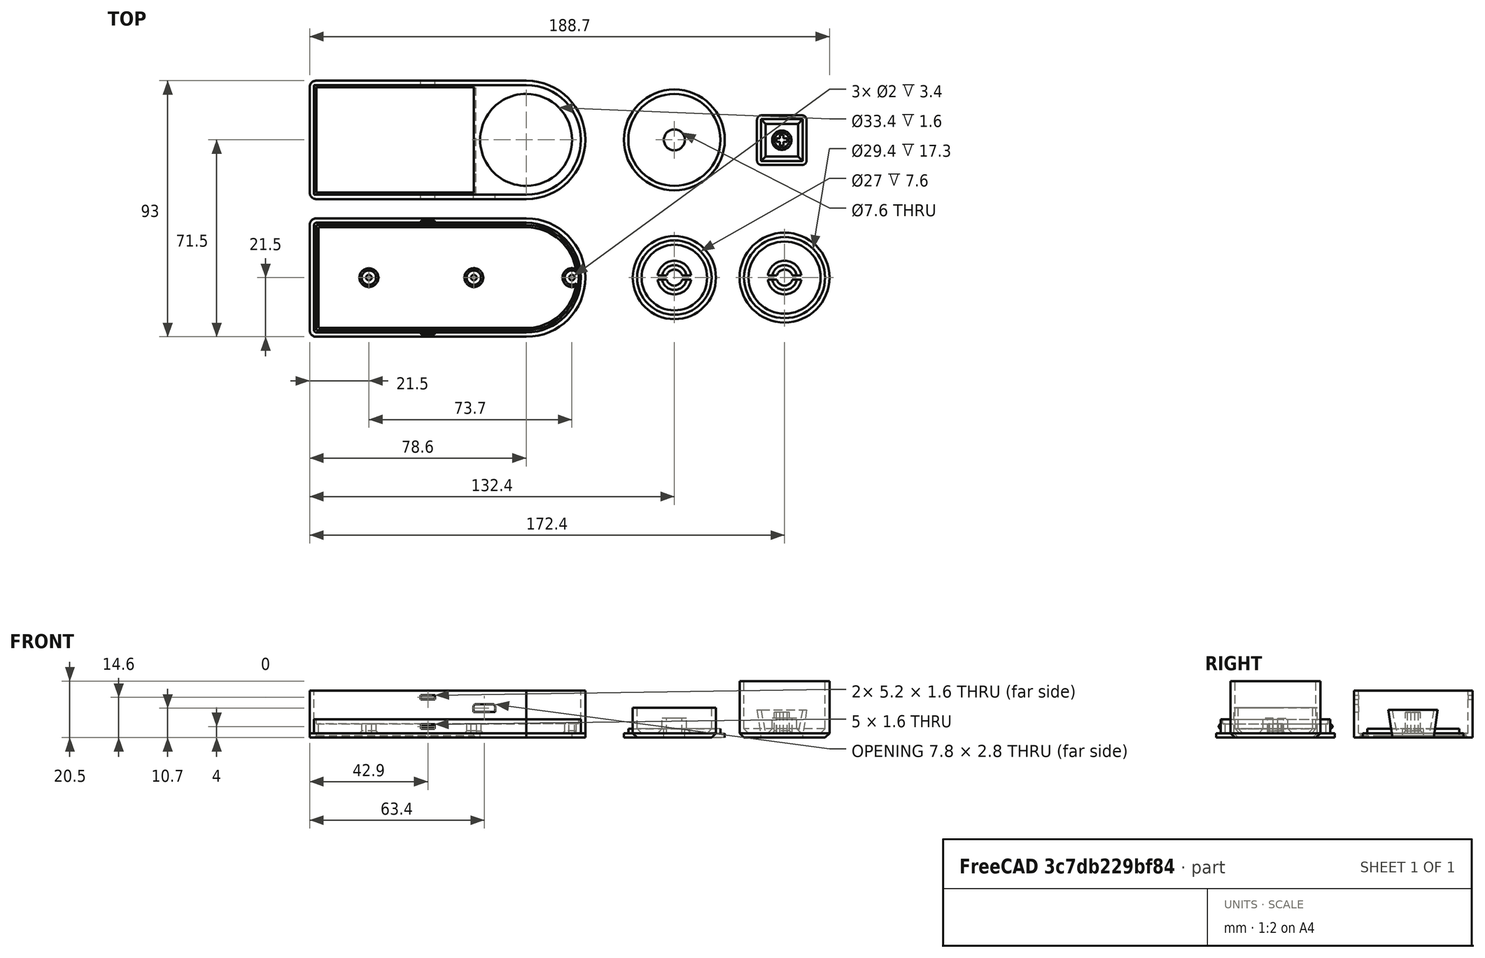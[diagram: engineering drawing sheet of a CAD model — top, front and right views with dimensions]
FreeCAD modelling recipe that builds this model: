
FCSTD DOCUMENT  (FreeCAD 0.16R)
Label: Macropad_plus
License: All rights reserved
LicenseURL: http://en.wikipedia.org/wiki/All_rights_reserved
objects: Part::Cylinder×25, Part::Cut×18, Part::Box×15, Part::MultiFuse×15, Part::Chamfer×13, Part::Fillet×5, Part::Wedge×2
note: 93 computed .brp shape members not serialized (recipe doc carries the construction recipe); baked Part::Feature solids carry a one-line shape summary decoded from their .brp

FEATURE [Part::Box] Box  label="Würfel"
  Height = 1.6
  Length = 78.7
  Placement = pos=(-2.4,-2.4,0) rot=(0,0,1;0rad)
  Width = 43
FEATURE [Part::Box] Box001  label="Würfel001"
  Height = 6.6
  Length = 77.1
  Placement = pos=(-0.8,-0.8,0) rot=(0,0,1;0rad)
  Width = 39.8
FEATURE [Part::Box] Box002  label="Würfel002"
  Height = 1.6
  Length = 76.3
  Placement = pos=(0,0,5) rot=(0,0,1;0rad)
  Width = 38.2
FEATURE [Part::Cylinder] Cylinder  label="Zylinder"
  Angle = 360
  Height = 1.6
  Placement = pos=(76.2,19.1,0) rot=(0,0,1;0rad)
  Radius = 21.5
FEATURE [Part::Cylinder] Cylinder001  label="Zylinder001"
  Angle = 360
  Height = 6.6
  Placement = pos=(76.2,19.1,0) rot=(0,0,1;0rad)
  Radius = 19.9
FEATURE [Part::Cylinder] Cylinder002  label="Zylinder002"
  Angle = 360
  Height = 1.6
  Placement = pos=(76.2,19.1,5) rot=(0,0,1;0rad)
  Radius = 19.1
FEATURE [Part::Box] Box003  label="Würfel003"
  Height = 5
  Length = 75.5
  Placement = pos=(0.8,0.8,1.6) rot=(0,0,1;0rad)
  Width = 36.6
FEATURE [Part::Cylinder] Cylinder003  label="Zylinder003"
  Angle = 360
  Height = 5
  Placement = pos=(76.2,19.1,1.6) rot=(0,0,1;0rad)
  Radius = 18.3
FEATURE [Part::MultiFuse] Fusion
  Shapes = -> [Box,Cylinder]
FEATURE [Part::MultiFuse] Fusion001
  Shapes = -> [Box001,Cylinder001]
FEATURE [Part::MultiFuse] Fusion002
  Shapes = -> [Box002,Cylinder002]
FEATURE [Part::MultiFuse] Fusion003
  Shapes = -> [Box003,Cylinder003]
FEATURE [Part::MultiFuse] Fusion004
  Shapes = -> [Fusion,Fusion001]
FEATURE [Part::MultiFuse] Fusion005
  Shapes = -> [Fusion002,Fusion003]
FEATURE [Part::Cut] Cut
  Base = -> Fusion004
  Tool = -> Fusion005
FEATURE [Part::Fillet] Fillet
  Base = -> Cut
  Edges = 2 edges r=0.8: [Edge30,Edge31]
FEATURE [Part::Fillet] Fillet001
  Base = -> Fillet
  Edges = 2 edges r=2.4: [Edge24,Edge27]
FEATURE [Part::Cylinder] Cylinder004  label="Zylinder004"
  Angle = 360
  Height = 5
  Placement = pos=(19.1,19.1,0) rot=(0,0,1;0rad)
  Radius = 2.6
FEATURE [Part::Cylinder] Cylinder005  label="Zylinder005"
  Angle = 360
  Height = 5
  Placement = pos=(19.1,19.1,1.6) rot=(0,0,1;0rad)
  Radius = 1
FEATURE [Part::Cut] Cut001
  Base = -> Cylinder004
  Tool = -> Cylinder005
FEATURE [Part::Cylinder] Cylinder006  label="Zylinder006"
  Angle = 360
  Height = 5
  Placement = pos=(57.2,19.1,0) rot=(0,0,1;0rad)
  Radius = 2.6
FEATURE [Part::Cylinder] Cylinder007  label="Zylinder007"
  Angle = 360
  Height = 5
  Placement = pos=(57.2,19.1,1.6) rot=(0,0,1;0rad)
  Radius = 1
FEATURE [Part::Cut] Cut002
  Base = -> Cylinder006
  Tool = -> Cylinder007
FEATURE [Part::Cylinder] Cylinder008  label="Zylinder008"
  Angle = 360
  Height = 5
  Placement = pos=(92.8,19.1,0) rot=(0,0,1;0rad)
  Radius = 2.6
FEATURE [Part::Cylinder] Cylinder009  label="Zylinder009"
  Angle = 360
  Height = 5
  Placement = pos=(92.8,19.1,1.6) rot=(0,0,1;0rad)
  Radius = 1
FEATURE [Part::Cut] Cut003
  Base = -> Cylinder008
  Tool = -> Cylinder009
FEATURE [Part::MultiFuse] Fusion006
  Shapes = -> [Fillet001,Cut002,Cut001,Cut003]
FEATURE [Part::Chamfer] Chamfer
  Base = -> Fusion006
  Edges = 1 edges r=0.8: [Edge178]
FEATURE [Part::Chamfer] Chamfer001
  Base = -> Chamfer
  Edges = 1 edges r=0.8: [Edge4]
FEATURE [Part::Chamfer] Chamfer002
  Base = -> Chamfer001
  Edges = 1 edges r=0.8: [Edge33]
FEATURE [Part::Box] Box004  label="Würfel004"
  Height = 1.6
  Length = 5
  Placement = pos=(38,39,3.2) rot=(0,0,1;0rad)
  Width = 0.8
FEATURE [Part::Box] Box005  label="Würfel005"
  Height = 1.6
  Length = 5
  Placement = pos=(38,-1.6,3.2) rot=(0,0,1;0rad)
  Width = 0.8
FEATURE [Part::Chamfer] Chamfer003
  Base = -> Box005
  Edges = 2 edges r=0.6: [Edge9,Edge10]
FEATURE [Part::Chamfer] Chamfer004
  Base = -> Box004
  Edges = 2 edges r=0.6: [Edge11,Edge12]
FEATURE [Part::MultiFuse] Fusion007  label="Bottom"
  Shapes = -> [Chamfer002,Chamfer003,Chamfer004]
FEATURE [Part::Box] Box006  label="Würfel006"
  Height = 17
  Length = 78.7
  Placement = pos=(-2.4,47.6,0) rot=(0,0,1;0rad)
  Width = 43
FEATURE [Part::Cylinder] Cylinder010  label="Zylinder010"
  Angle = 360
  Height = 17
  Placement = pos=(76.2,69.1,0) rot=(0,0,1;0rad)
  Radius = 21.5
FEATURE [Part::Box] Box007  label="Würfel007"
  Height = 17
  Length = 77.1
  Placement = pos=(-0.8,49.2,1.6) rot=(0,0,1;0rad)
  Width = 39.8
FEATURE [Part::Cylinder] Cylinder011  label="Zylinder011"
  Angle = 360
  Height = 17
  Placement = pos=(76.2,69.1,1.6) rot=(0,0,1;0rad)
  Radius = 19.9
FEATURE [Part::MultiFuse] Fusion008
  Shapes = -> [Box006,Cylinder010]
FEATURE [Part::MultiFuse] Fusion009
  Shapes = -> [Box007,Cylinder011]
FEATURE [Part::Cut] Cut004
  Base = -> Fusion008
  Tool = -> Fusion009
FEATURE [Part::Fillet] Fillet002
  Base = -> Cut004
  Edges = 2 edges r=2.4: [Edge1,Edge3]
FEATURE [Part::Cylinder] Cylinder012  label="Zylinder012"
  Angle = 360
  Height = 1.6
  Placement = pos=(76.2,69.1,0) rot=(0,0,1;0rad)
  Radius = 16.7
FEATURE [Part::Box] Box008  label="Würfel008"
  Height = 1.6
  Length = 57.2
  Placement = pos=(0,50,0) rot=(0,0,1;0rad)
  Width = 38.2
FEATURE [Part::Cut] Cut005
  Base = -> Fillet002
  Tool = -> Cylinder012
FEATURE [Part::Cut] Cut006
  Base = -> Cut005
  Tool = -> Box008
FEATURE [Part::Chamfer] Chamfer005
  Base = -> Cut006
  Edges = 6 edges r=0.8: [Edge20,Edge21,Edge22,Edge23,Edge24,Edge47]
FEATURE [Part::Cylinder] Cylinder013  label="Zylinder013"
  Angle = 360
  Height = 3.2
  Placement = pos=(130,69.1,0) rot=(0,0,1;0rad)
  Radius = 16.7
FEATURE [Part::Cylinder] Cylinder014  label="Zylinder014"
  Angle = 360
  Height = 1.6
  Placement = pos=(130,69.1,0) rot=(0,0,1;0rad)
  Radius = 18.3
FEATURE [Part::MultiFuse] Fusion010
  Shapes = -> [Cylinder013,Cylinder014]
FEATURE [Part::Cylinder] Cylinder015  label="Zylinder015"
  Angle = 360
  Height = 3.2
  Placement = pos=(130,69.1,0) rot=(0,0,1;0rad)
  Radius = 3.8
FEATURE [Part::Cut] Cut007  label="Ring"
  Base = -> Fusion010
  Tool = -> Cylinder015
FEATURE [Part::Cylinder] Cylinder016  label="Zylinder016"
  Angle = 360
  Height = 10.8
  Placement = pos=(130,19.1,0) rot=(0,0,1;0rad)
  Radius = 15.1
FEATURE [Part::Cylinder] Cylinder017  label="Zylinder017"
  Angle = 360
  Height = 10.8
  Placement = pos=(130,19.1,1.6) rot=(0,0,1;0rad)
  Radius = 13.5
FEATURE [Part::Cut] Cut008
  Base = -> Cylinder016
  Tool = -> Cylinder017
FEATURE [Part::Chamfer] Chamfer006
  Base = -> Cut008
  Edges = 1 edges r=1.6: [Edge6]
FEATURE [Part::Chamfer] Chamfer007
  Base = -> Chamfer006
  Edges = 1 edges r=1.6: [Edge8]
FEATURE [Part::Cylinder] Cylinder018  label="Zylinder018"
  Angle = 360
  Height = 7
  Placement = pos=(130,19.1,0) rot=(0,0,1;0rad)
  Radius = 4.5
FEATURE [Part::Cylinder] Cylinder019  label="Zylinder019"
  Angle = 360
  Height = 10.5
  Placement = pos=(130,19.1,1.6) rot=(0,0,1;0rad)
  Radius = 2.9
FEATURE [Part::Cut] Cut009
  Base = -> Cylinder018
  Tool = -> Cylinder019
FEATURE [Part::MultiFuse] Fusion011
  Shapes = -> [Chamfer007,Cut009]
FEATURE [Part::Chamfer] Chamfer008
  Base = -> Fusion011
  Edges = 1 edges r=1.6: [Edge12]
FEATURE [Part::Box] Box009  label="Würfel009"
  Height = 10.5
  Length = 15
  Placement = pos=(123,18.3,1.6) rot=(0,0,1;0rad)
  Width = 1.6
FEATURE [Part::Cut] Cut010  label="Knob"
  Base = -> Chamfer008
  Tool = -> Box009
FEATURE [Part::Box] Box010  label="Würfel010"
  Height = 1.6
  Length = 5.2
  Placement = pos=(37.9,45,13.8) rot=(0,0,1;0rad)
  Width = 50
FEATURE [Part::Cut] Cut011
  Base = -> Chamfer005
  Tool = -> Box010
FEATURE [Part::Box] Box011  label="Würfel011"
  Height = 2.8
  Length = 7.8
  Placement = pos=(57.1,45,9.3) rot=(0,0,1;0rad)
  Width = 10
FEATURE [Part::Fillet] Fillet003  label="USB"
  Base = -> Box011
  Edges = 2 edges r=0.8: [Edge2,Edge6]
FEATURE [Part::Cut] Cut012  label="Top"
  Base = -> Cut011
  Tool = -> Fillet003
FEATURE [Part::Wedge] Wedge  label="Keil"
  Placement = pos=(170,20,10) rot=(-1,0,0;1.5708rad)
  X2max = 16.5
  X2min = 1.5
  Xmax = 18
  Xmin = 0
  Ymax = 10
  Ymin = 0
  Z2max = 16.5
  Z2min = 1.5
  Zmax = 18
  Zmin = 0
FEATURE [Part::Wedge] Wedge001  label="Keil001"
  Placement = pos=(171.4,21.4,10) rot=(-1,0,0;1.5708rad)
  X2max = 13.5
  X2min = 1.7
  Xmax = 15.2
  Xmin = 0
  Ymax = 8.4
  Ymin = 0
  Z2max = 13.5
  Z2min = 1.7
  Zmax = 15.2
  Zmin = 0
FEATURE [Part::Cut] Cut013
  Base = -> Wedge
  Tool = -> Wedge001
FEATURE [Part::Fillet] Fillet004
  Base = -> Cut013
  Edges = 4 edges r=1.6: [Edge2,Edge4,Edge13,Edge16]
FEATURE [Part::Cylinder] Cylinder020  label="Zylinder020"
  Angle = 360
  Height = 9.2
  Placement = pos=(179,29,0) rot=(0,0,1;0rad)
  Radius = 2.7
FEATURE [Part::MultiFuse] Fusion012
  Shapes = -> [Fillet004,Cylinder020]
FEATURE [Part::Chamfer] Chamfer009
  Base = -> Fusion012
  Edges = 1 edges r=0.8: [Edge3]
FEATURE [Part::Box] Box012  label="Würfel012"
  Height = 10
  Length = 4
  Placement = pos=(177,28.35,1.6) rot=(0,0,1;0rad)
  Width = 1.3
FEATURE [Part::Box] Box013  label="Würfel013"
  Height = 10
  Length = 4
  Placement = pos=(179.65,27,1.6) rot=(0,0,1;1.5708rad)
  Width = 1.3
FEATURE [Part::MultiFuse] Fusion013
  Shapes = -> [Box012,Box013]
FEATURE [Part::Cut] Cut014  label="Keycap"
  Base = -> Chamfer009
  Placement = pos=(-10,40,0) rot=(0,0,1;0rad)
  Tool = -> Fusion013
FEATURE [Part::Cylinder] Cylinder021  label="Zylinder021"
  Angle = 360
  Height = 20.5
  Placement = pos=(130,19.1,0) rot=(0,0,1;0rad)
  Radius = 16.3
FEATURE [Part::Cylinder] Cylinder022  label="Zylinder022"
  Angle = 360
  Height = 20.5
  Placement = pos=(130,19.1,1.6) rot=(0,0,1;0rad)
  Radius = 14.7
FEATURE [Part::Cut] Cut015
  Base = -> Cylinder021
  Tool = -> Cylinder022
FEATURE [Part::Chamfer] Chamfer010
  Base = -> Cut015
  Edges = 1 edges r=1.6: [Edge6]
FEATURE [Part::Chamfer] Chamfer011
  Base = -> Chamfer010
  Edges = 1 edges r=1.6: [Edge8]
FEATURE [Part::Cylinder] Cylinder023  label="Zylinder023"
  Angle = 360
  Height = 7
  Placement = pos=(130,19.1,0) rot=(0,0,1;0rad)
  Radius = 4.5
FEATURE [Part::Cylinder] Cylinder024  label="Zylinder024"
  Angle = 360
  Height = 10.5
  Placement = pos=(130,19.1,1.6) rot=(0,0,1;0rad)
  Radius = 2.9
FEATURE [Part::Cut] Cut016
  Base = -> Cylinder023
  Tool = -> Cylinder024
FEATURE [Part::MultiFuse] Fusion014
  Shapes = -> [Chamfer011,Cut016]
FEATURE [Part::Chamfer] Chamfer012
  Base = -> Fusion014
  Edges = 1 edges r=1.6: [Edge12]
FEATURE [Part::Box] Box014  label="Würfel014"
  Height = 10.5
  Length = 15
  Placement = pos=(123,18.3,1.6) rot=(0,0,1;0rad)
  Width = 1.6
FEATURE [Part::Cut] Cut017  label="Knob_big"
  Base = -> Chamfer012
  Placement = pos=(40,0,0) rot=(0,0,1;0rad)
  Tool = -> Box014
